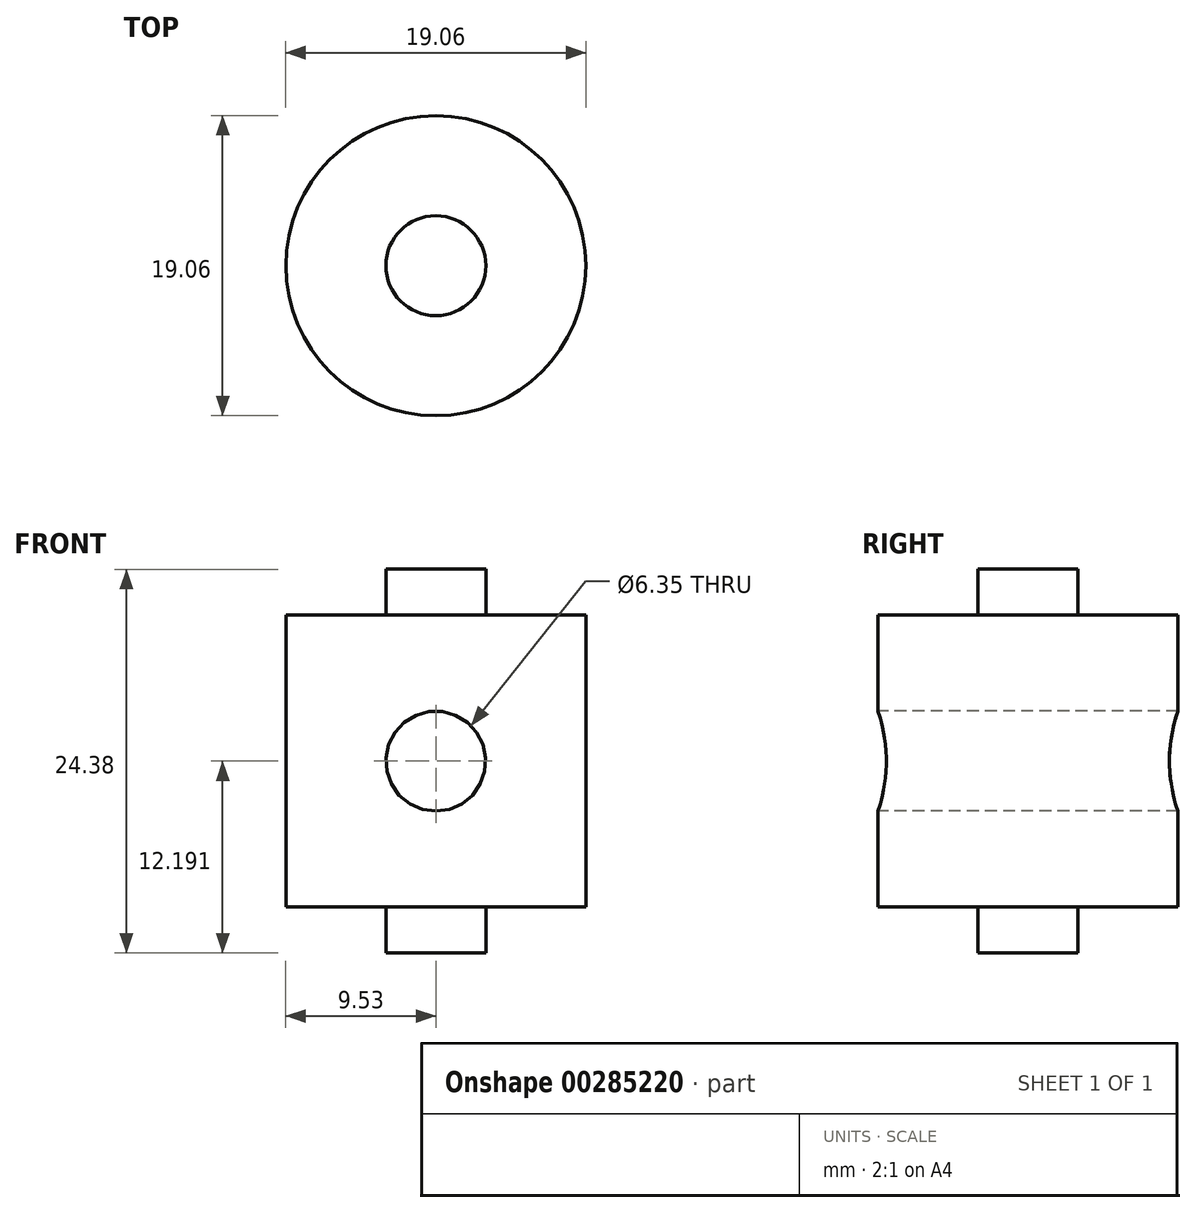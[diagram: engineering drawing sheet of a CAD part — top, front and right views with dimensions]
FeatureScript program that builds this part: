
annotation { "Feature Type Name" : "Feature", "Feature Type Description" : "" }
export const myFeature = defineFeature(function(context is Context, id is Id, definition is map)
    precondition{}
    {
        {
            var Q0;
            Q0=qCreatedBy(makeId("Top.planeOp"),FACE);
            var sketch = newSketch(context, id + "F0", { "sketchPlane" : qUnion([Q0])});
            skCircle(sketch, "E0", {"center": v(0, 0) * mm, "radius": 9.53 * mm});
            skSolve(sketch);
        }
        {
            var Q0;
            Q0 = qSketchRegion(id + "F0", true);
            extrude(context, id + "F1", {"entities" : qUnion([Q0]), "depth" : 18.54 * mm});
        }
        {
            var Q0;
            Q0=makeQuery(id+"F1.opExtrude","CAP_FACE",FACE,{"disambiguationData":[OSD([sQuery(id+"F0.wireOp",EDGE,"E0")])],"isStart":false});
            var sketch = newSketch(context, id + "F2", { "sketchPlane" : qUnion([Q0])});
            skCircle(sketch, "E1", {"center": v(0, 0) * mm, "radius": 3.18 * mm});
            skSolve(sketch);
        }
        {
            var Q0;
            Q0 = qSketchRegion(id + "F2", true);
            extrude(context, id + "F3", {"entities" : qUnion([Q0]), "operationType" : NewBodyOperationType.ADD, "depth" : 2.92 * mm});
        }
        {
            var Q0;
            Q0=makeQuery(id+"F1.opExtrude","CAP_FACE",FACE,{"disambiguationData":[OSD([sQuery(id+"F0.wireOp",EDGE,"E0")])],"isStart":true});
            var sketch = newSketch(context, id + "F4", { "sketchPlane" : qUnion([Q0])});
            skCircle(sketch, "E2", {"center": v(0, 0) * mm, "radius": 3.18 * mm});
            skSolve(sketch);
        }
        {
            var Q0;
            Q0 = qSketchRegion(id + "F4", true);
            extrude(context, id + "F5", {"entities" : qUnion([Q0]), "operationType" : NewBodyOperationType.ADD, "depth" : 2.92 * mm});
        }
        {
            var Q0;
            Q0=qCreatedBy(makeId("Front.planeOp"),FACE);
            var sketch = newSketch(context, id + "F6", { "sketchPlane" : qUnion([Q0])});
            skLineSegment(sketch, "E3", {"start": v(-9.53, 0) * mm, "end": v(-9.53, 18.54) * mm});
            skLineSegment(sketch, "E4", {"start": v(9.53, 18.54) * mm, "end": v(9.53, 0) * mm});
            skLineSegment(sketch, "E5", {"start": v(-9.52, 18.54) * mm, "end": v(9.52, 0) * mm, "construction": true});
            skCircle(sketch, "E6", {"center": v(0, 9.27) * mm, "radius": 3.18 * mm});
            skSolve(sketch);
        }
        {
            var Q0;
            Q0 = qSketchRegion(id + "F6", true);
            extrude(context, id + "F7", {"entities" : qUnion([Q0]), "operationType" : NewBodyOperationType.REMOVE, "oppositeDirection" : true, "depth" : 25.4 * mm, "hasSecondDirection" : true, "secondDirectionOppositeDirection" : false, "secondDirectionDepth" : 25.4 * mm});
        }
    });
